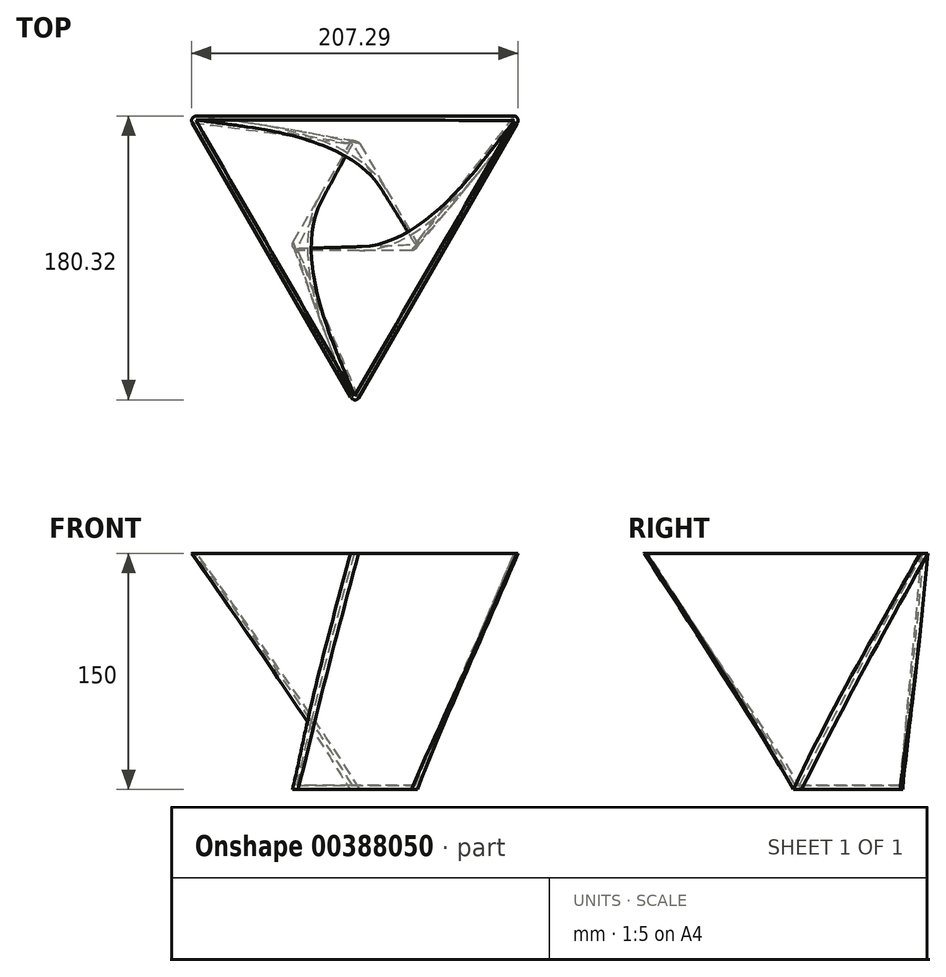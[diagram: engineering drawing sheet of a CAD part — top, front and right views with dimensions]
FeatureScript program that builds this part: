
annotation { "Feature Type Name" : "Feature", "Feature Type Description" : "" }
export const myFeature = defineFeature(function(context is Context, id is Id, definition is map)
    precondition{}
    {
        {
            var Q0;
            Q0=qCreatedBy(makeId("Top.planeOp"),FACE);
            var sketch = newSketch(context, id + "F0", { "sketchPlane" : qUnion([Q0])});
            skCircle(sketch, "E0.cCircle", {"center": v(0, 0) * mm, "radius": 24.45 * mm, "construction": true});
            skLineSegment(sketch, "E0.0", {"start": v(42.34, -24.45) * mm, "end": v(-42.34, -24.45) * mm});
            skLineSegment(sketch, "E0.1", {"start": v(-42.34, -24.45) * mm, "end": v(0, 48.9) * mm});
            skLineSegment(sketch, "E0.2", {"start": v(0, 48.9) * mm, "end": v(42.34, -24.45) * mm});
            skPoint(sketch, "E0.0.midPoint", {"position": v(0, -24.45) * mm});
            skSolve(sketch);
        }
        {
            var Q0;
            Q0=qCreatedBy(makeId("Top.planeOp"),FACE);
            cPlane(context, id + "F1", {"entities" : qUnion([Q0]), "cplaneType" : CPlaneType.OFFSET, "offset" : 150 * mm, "width" : 150 * mm, "height" : 150 * mm});
        }
        {
            var Q0;
            Q0=qCreatedBy(id+"F1.planeOp",FACE);
            var sketch = newSketch(context, id + "F2", { "sketchPlane" : qUnion([Q0])});
            skCircle(sketch, "E1.cCircle", {"center": v(0, 0) * mm, "radius": 61.06 * mm, "construction": true});
            skLineSegment(sketch, "E1.0", {"start": v(-105.76, 61.06) * mm, "end": v(105.76, 61.06) * mm});
            skLineSegment(sketch, "E1.1", {"start": v(105.76, 61.06) * mm, "end": v(0, -122.13) * mm});
            skLineSegment(sketch, "E1.2", {"start": v(0, -122.13) * mm, "end": v(-105.76, 61.06) * mm});
            skPoint(sketch, "E1.0.midPoint", {"position": v(0, 61.06) * mm});
            skSolve(sketch);
        }
        {
            var Q0;
            Q0 = qSketchRegion(id + "F0", true);
            var Q1;
            Q1 = qSketchRegion(id + "F2", true);
            loft(context, id + "F3", {"sheetProfilesArray" : [{ "sheetProfileEntities" : qUnion([Q0]) }, { "sheetProfileEntities" : qUnion([Q1]) }]});
        }
        {
            var Q0;
            Q0=makeQuery(id+"F3.opLoft","CAP_FACE",FACE,{"disambiguationData":[OSD([makeQuery(id+"F2.imprint","IMPRINT",FACE,{"disambiguationData":[TD([[makeQuery(id+"F2.imprint","IMPRINT",EDGE,{"derivedFrom":sQuery(id+"F2.wireOp",EDGE,"E1.0")}),-1.0]])]})])],"isStart":true});
            shell(context, id + "F4", {"entities" : qUnion([Q0]), "thickness" : 2.5 * mm});
        }
        {
            var Q0;
            Q0=makeQuery(id+"F3.opLoft","SWEPT_EDGE",EDGE,{"disambiguationData":[OSD([sQuery(id+"F0.wireOp",EDGE,"E0.0"),sQuery(id+"F0.wireOp",EDGE,"E0.2"),sQuery(id+"F2.wireOp",EDGE,"E1.1"),sQuery(id+"F2.wireOp",EDGE,"E1.2")])]});
            var Q1;
            Q1=makeQuery(id+"F3.opLoft","SWEPT_EDGE",EDGE,{"disambiguationData":[OSD([sQuery(id+"F0.wireOp",EDGE,"E0.1"),sQuery(id+"F0.wireOp",EDGE,"E0.2"),sQuery(id+"F2.wireOp",EDGE,"E1.0"),sQuery(id+"F2.wireOp",EDGE,"E1.1")])]});
            var Q2;
            Q2=makeQuery(id+"F3.opLoft","SWEPT_EDGE",EDGE,{"disambiguationData":[OSD([sQuery(id+"F0.wireOp",EDGE,"E0.0"),sQuery(id+"F0.wireOp",EDGE,"E0.1"),sQuery(id+"F2.wireOp",EDGE,"E1.0"),sQuery(id+"F2.wireOp",EDGE,"E1.2")])]});
            fillet(context, id + "F5", {"entities" : qUnion([Q0, Q1, Q2]), "radius" : 3 * mm, "tangentPropagation" : true, "allowEdgeOverflow" : false});
        }
    });
